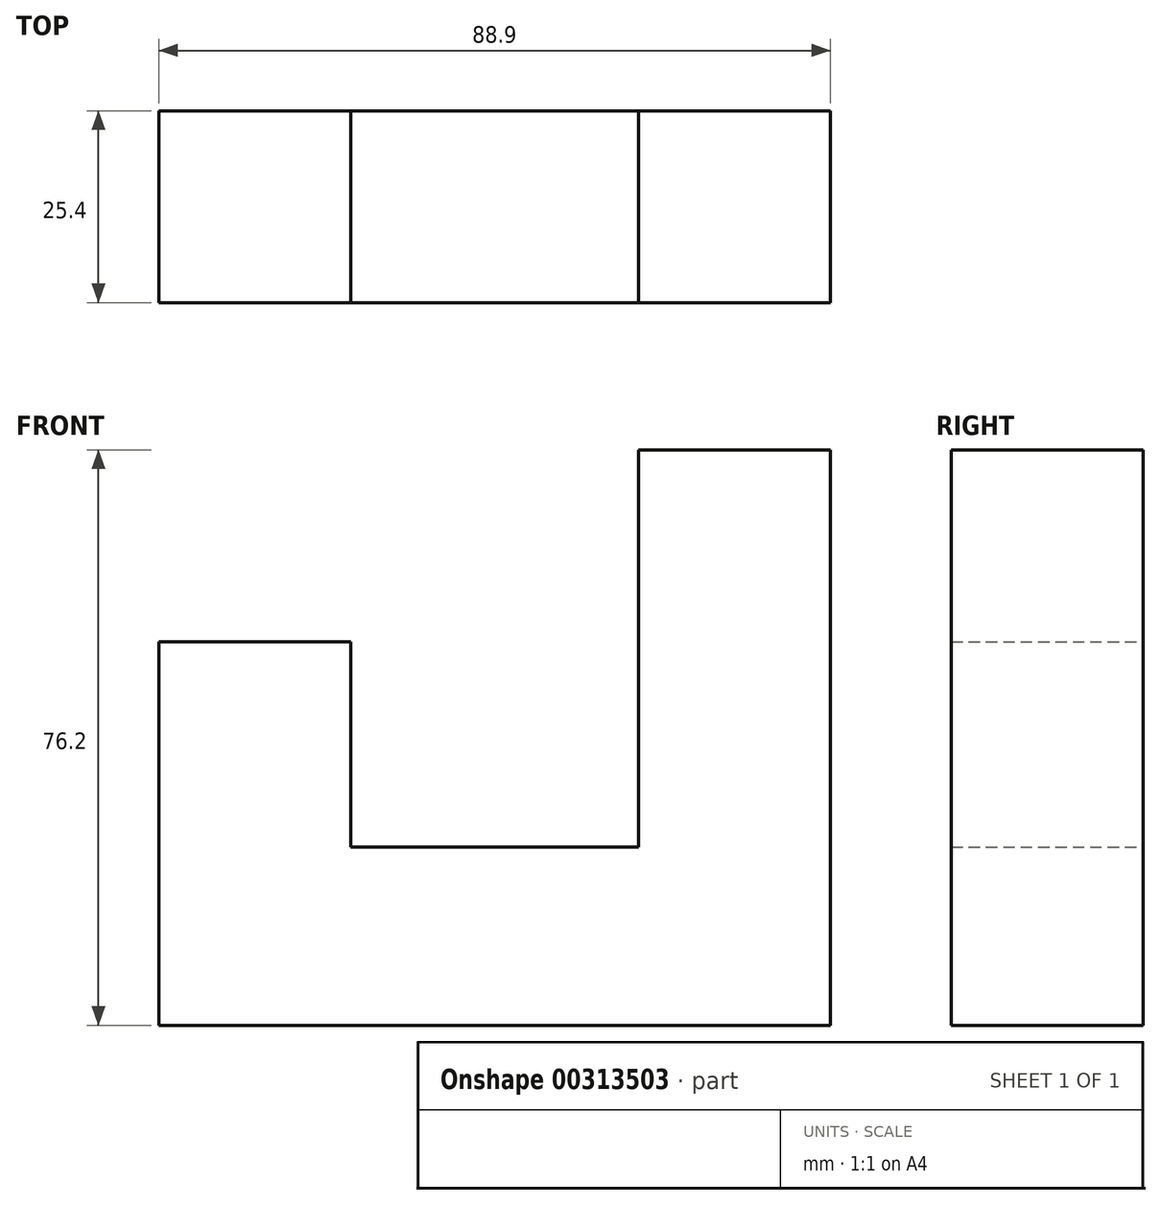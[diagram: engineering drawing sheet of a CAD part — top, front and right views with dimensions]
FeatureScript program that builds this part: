
annotation { "Feature Type Name" : "Feature", "Feature Type Description" : "" }
export const myFeature = defineFeature(function(context is Context, id is Id, definition is map)
    precondition{}
    {
        {
            var Q0;
            Q0=qCreatedBy(makeId("Front.planeOp"),FACE);
            var sketch = newSketch(context, id + "F0", { "sketchPlane" : qUnion([Q0])});
            skLineSegment(sketch, "E0", {"start": v(-56.97, -20.96) * mm, "end": v(31.93, -20.96) * mm});
            skLineSegment(sketch, "E1", {"start": v(-31.57, 2.66) * mm, "end": v(6.53, 2.66) * mm});
            skLineSegment(sketch, "E2", {"start": v(31.93, -20.96) * mm, "end": v(31.93, 55.24) * mm});
            skLineSegment(sketch, "E3", {"start": v(31.93, 55.24) * mm, "end": v(6.53, 55.24) * mm});
            skLineSegment(sketch, "E4", {"start": v(6.53, 2.66) * mm, "end": v(6.53, 55.24) * mm});
            skLineSegment(sketch, "E5", {"start": v(-31.57, 2.66) * mm, "end": v(-31.57, 29.84) * mm});
            skLineSegment(sketch, "E6", {"start": v(-31.57, 29.84) * mm, "end": v(-56.97, 29.84) * mm});
            skLineSegment(sketch, "E7", {"start": v(-56.97, 29.84) * mm, "end": v(-56.97, -20.96) * mm});
            skSolve(sketch);
        }
        {
            var Q0;
            Q0=makeQuery(id+"F0.imprint","IMPRINT",FACE,{"disambiguationData":[TD([[makeQuery(id+"F0.imprint","IMPRINT",EDGE,{"derivedFrom":sQuery(id+"F0.wireOp",EDGE,"E0")}),1.0]])]});
            extrude(context, id + "F1", {"entities" : qUnion([Q0]), "depth" : 25.4 * mm});
        }
    });
